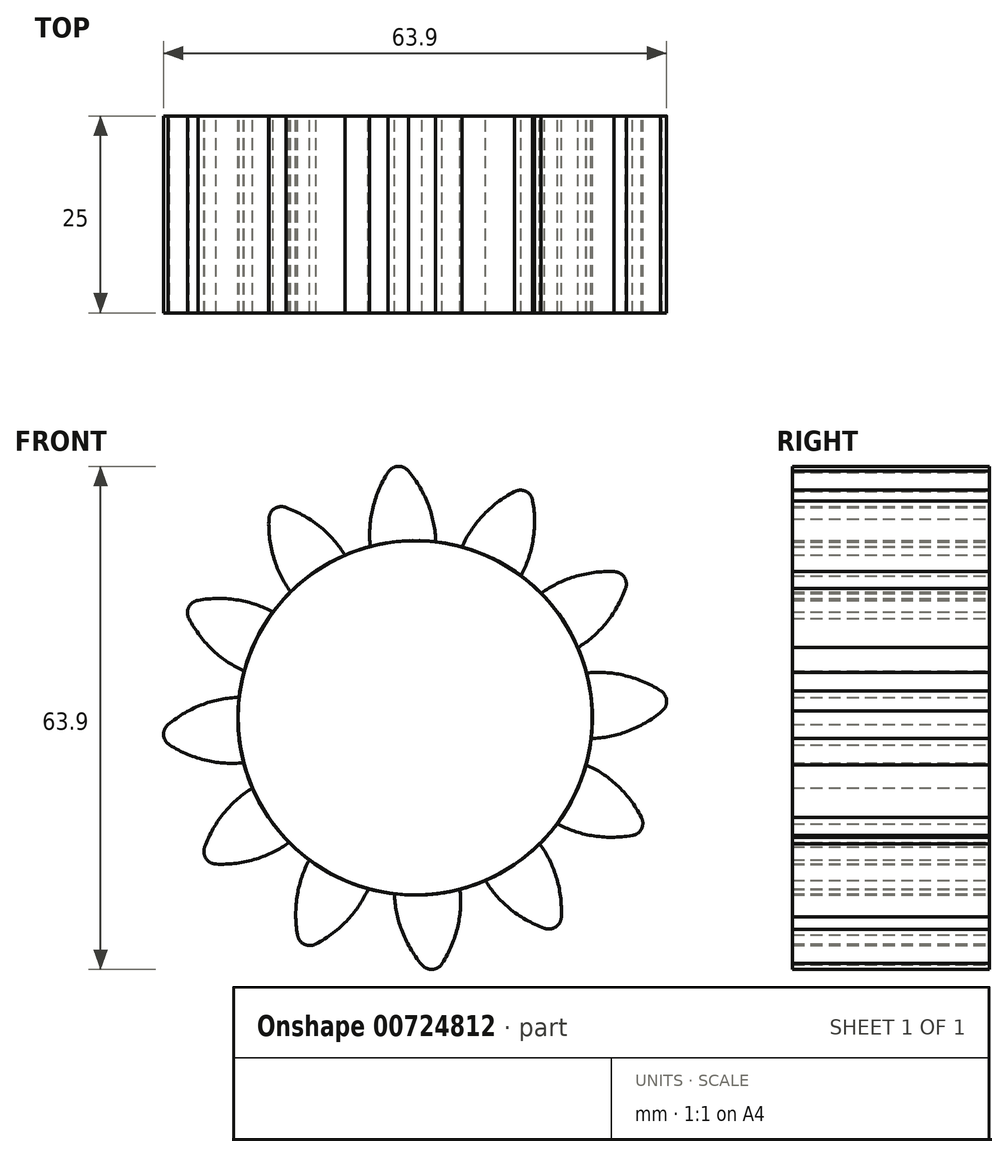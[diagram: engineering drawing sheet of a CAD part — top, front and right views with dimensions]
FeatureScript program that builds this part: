
annotation { "Feature Type Name" : "Feature", "Feature Type Description" : "" }
export const myFeature = defineFeature(function(context is Context, id is Id, definition is map)
    precondition{}
    {
        {
            var Q0;
            Q0=qCreatedBy(makeId("Front.planeOp"),FACE);
            var sketch = newSketch(context, id + "F0", { "sketchPlane" : qUnion([Q0])});
            skCircle(sketch, "E0", {"center": v(4.6, -19.32) * mm, "radius": 22.51 * mm});
            skCircle(sketch, "E1", {"center": v(4.6, -19.32) * mm, "radius": 27.14 * mm, "construction": true});
            skCircle(sketch, "E2", {"center": v(4.6, -19.32) * mm, "radius": 35.8 * mm, "construction": true});
            skLineSegment(sketch, "E3", {"start": v(4.6, -19.32) * mm, "end": v(4.6, 54.18) * mm, "construction": true});
            skLineSegment(sketch, "E4", {"start": v(4.6, -19.32) * mm, "end": v(-1.5, 54.18) * mm, "construction": true});
            skLineSegment(sketch, "E5", {"start": v(4.6, 7.82) * mm, "end": v(-45.62, 7.82) * mm, "construction": true});
            skLineSegment(sketch, "E6", {"start": v(4.6, 7.82) * mm, "end": v(-45.62, -10.46) * mm, "construction": true});
            skCircle(sketch, "E7", {"center": v(4.6, -19.32) * mm, "radius": 25.5 * mm, "construction": true});
            skCircle(sketch, "E8", {"center": v(4.6, 7.82) * mm, "radius": 14.6 * mm, "construction": true});
            skCircle(sketch, "E9", {"center": v(-9.12, 2.82) * mm, "radius": 14.6 * mm, "construction": true});
            skArc(sketch, "E10", {"start": v(4.6, 7.82) * mm, "mid": v(1.83, 12.45) * mm, "end": v(-2.4, 15.8) * mm});
            skLineSegment(sketch, "E11", {"start": v(4.49, -33.68) * mm, "end": v(4.6, -33.82) * mm});
            skLineSegment(sketch, "E12", {"start": v(4.6, -33.82) * mm, "end": v(4.72, -33.68) * mm});
            skLineSegment(sketch, "E13", {"start": v(4.6, -19.32) * mm, "end": v(-3.7, 107.5) * mm, "construction": true});
            skPoint(sketch, "E13.endSnap0", {"position": v(-3.7, -5.43) * mm});
            skArc(sketch, "E14", {"start": v(6.34, 7.58) * mm, "mid": v(5.24, 9.92) * mm, "end": v(3.75, 12.04) * mm});
            skArc(sketch, "E15", {"start": v(7.22, 2.94) * mm, "mid": v(6.97, 5.3) * mm, "end": v(6.34, 7.58) * mm});
            skArc(sketch, "E16.MirrorCS", {"start": v(-0.83, 7.1) * mm, "mid": v(-0.04, 9.57) * mm, "end": v(1.16, 11.87) * mm});
            skArc(sketch, "E17.MirrorCS", {"start": v(-1.09, 2.4) * mm, "mid": v(-1.16, 4.76) * mm, "end": v(-0.83, 7.1) * mm});
            skArc(sketch, "E18", {"start": v(3.75, 12.04) * mm, "mid": v(2.41, 12.63) * mm, "end": v(1.16, 11.87) * mm});
            skSolve(sketch);
        }
        {
            var Q0;
            {var subQ0=sQuery(id+"F0.wireOp",EDGE,"E0");var subQ1=makeQuery(id+"F0.imprint","INTERSECT",VERTEX,{"derivedFrom":[subQ0,sQuery(id+"F0.wireOp",EDGE,"E15")]});Q0=makeQuery(id+"F0.imprint","IMPRINT",FACE,{"disambiguationData":[TD([[makeQuery(id+"F0.imprint","IMPRINT",EDGE,{"disambiguationData":[TD([[subQ1,-1.0]])],"derivedFrom":subQ0}),1.0]])]});}
            var Q1;
            {var subQ2=sQuery(id+"F0.wireOp",EDGE,"E14");Q1=makeQuery(id+"F0.imprint","IMPRINT",FACE,{"disambiguationData":[TD([[makeQuery(id+"F0.imprint","IMPRINT",EDGE,{"derivedFrom":subQ2}),1.0]])]});}
            extrude(context, id + "F1", {"entities" : qUnion([Q0, Q1]), "depth" : 25 * mm, "offsetDistance" : 25 * mm});
        }
        {
            var Q0;
            Q0=makeQuery(id+"F1.opExtrude","SWEPT_BODY",BODY,{"disambiguationData":[OSD([sQuery(id+"F0.wireOp",EDGE,"E0"),sQuery(id+"F0.wireOp",EDGE,"E14"),sQuery(id+"F0.wireOp",EDGE,"E15"),sQuery(id+"F0.wireOp",EDGE,"E16.MirrorCS"),sQuery(id+"F0.wireOp",EDGE,"E17.MirrorCS"),sQuery(id+"F0.wireOp",EDGE,"E18")])]});
            var Q1;
            Q1=makeQuery(id+"F1.opExtrude","SWEPT_FACE",FACE,{"disambiguationData":[OSD([sQuery(id+"F0.wireOp",EDGE,"E0")])]});
            circularPattern(context, id + "F2", {"entities" : qUnion([Q0]), "axis" : qUnion([Q1]), "angle" : 360 * degree, "instanceCount" : 12, "equalSpace" : true});
        }
    });
